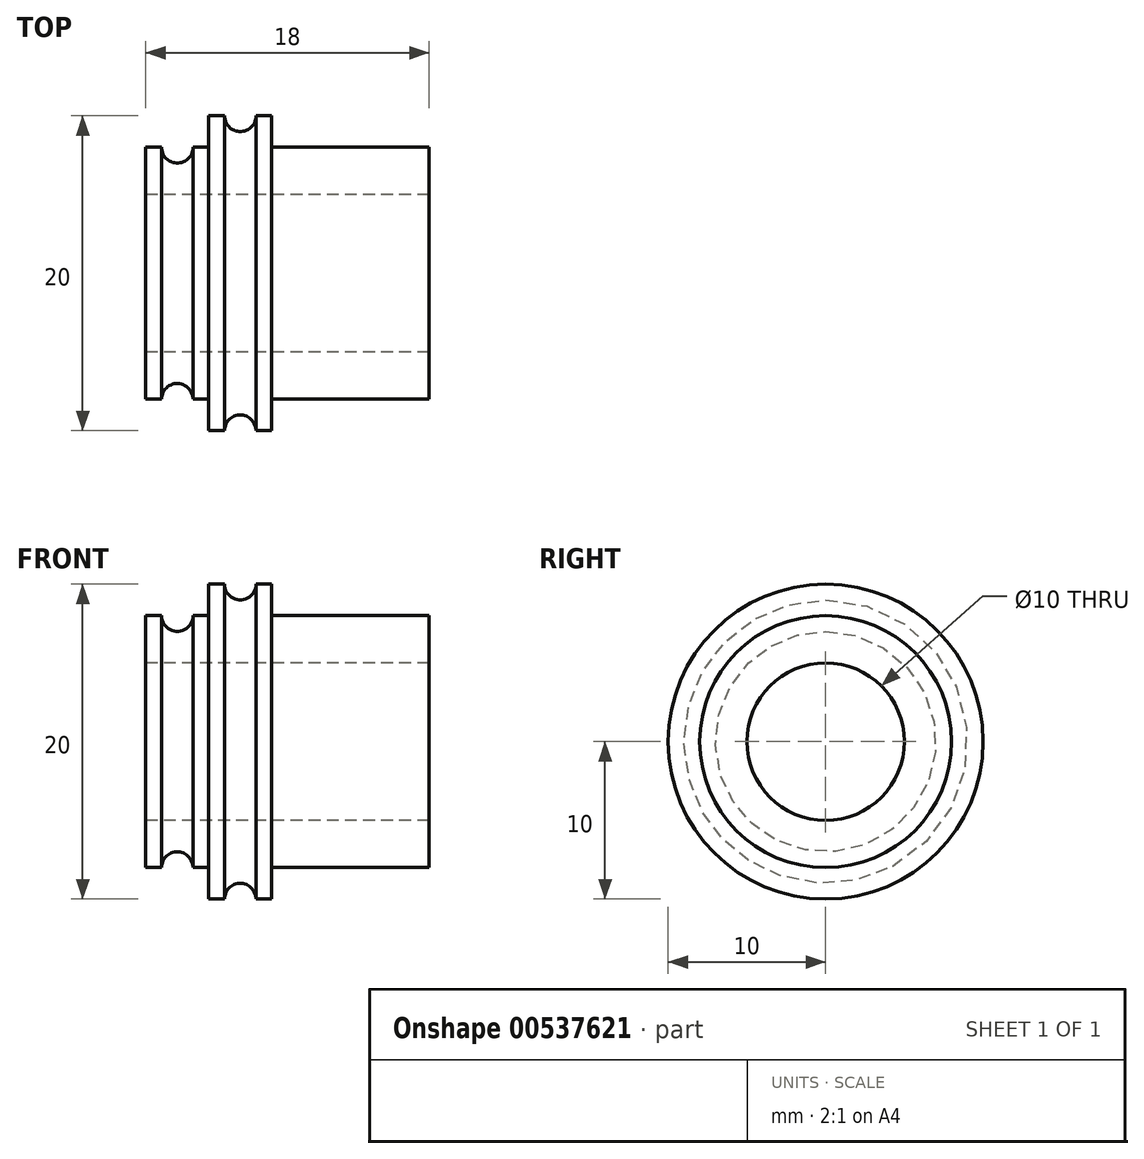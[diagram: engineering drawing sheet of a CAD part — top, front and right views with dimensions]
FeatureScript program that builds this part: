
annotation { "Feature Type Name" : "Feature", "Feature Type Description" : "" }
export const myFeature = defineFeature(function(context is Context, id is Id, definition is map)
    precondition{}
    {
        {
            var Q0;
            Q0=qCreatedBy(makeId("Front.planeOp"),FACE);
            var sketch = newSketch(context, id + "F0", { "sketchPlane" : qUnion([Q0])});
            skLineSegment(sketch, "E0.bottom", {"start": v(0, 5) * mm, "end": v(8, 5) * mm});
            skLineSegment(sketch, "E0.top", {"start": v(4, 10) * mm, "end": v(8, 10) * mm});
            skLineSegment(sketch, "E0.left", {"start": v(0, 5) * mm, "end": v(0, 8) * mm});
            skLineSegment(sketch, "E0.right", {"start": v(8, 5) * mm, "end": v(8, 10) * mm});
            skCircle(sketch, "E1", {"center": v(6, 10) * mm, "radius": 1 * mm});
            skLineSegment(sketch, "E2", {"start": v(0, 0) * mm, "end": v(5.49, 0) * mm});
            skLineSegment(sketch, "E3", {"start": v(0, 8) * mm, "end": v(4, 8) * mm});
            skLineSegment(sketch, "E4", {"start": v(4, 8) * mm, "end": v(4, 10) * mm});
            skPoint(sketch, "E5.orphan", {"position": v(0, 10) * mm});
            skCircle(sketch, "E6", {"center": v(2, 8) * mm, "radius": 1 * mm});
            skSolve(sketch);
        }
        {
            var Q0;
            Q0=makeQuery(id+"F0.imprint","IMPRINT",FACE,{"disambiguationData":[TD([[makeQuery(id+"F0.imprint","IMPRINT",EDGE,{"derivedFrom":sQuery(id+"F0.wireOp",EDGE,"E0.bottom")}),1.0]])]});
            var Q1;
            Q1=sQuery(id+"F0.wireOp",EDGE,"E2");
            revolve(context, id + "F1", {"entities" : qUnion([Q0]), "axis" : qUnion([Q1]), "revolveType" : RevolveType.FULL});
        }
        {
            var Q0;
            Q0=makeQuery(id+"F1.opRevolve","SWEPT_FACE",FACE,{"disambiguationData":[OSD([sQuery(id+"F0.wireOp",EDGE,"E0.right")])]});
            var sketch = newSketch(context, id + "F2", { "sketchPlane" : qUnion([Q0])});
            skCircle(sketch, "E7", {"center": v(0, 0) * mm, "radius": 8 * mm});
            skSolve(sketch);
        }
        {
            var Q0;
            Q0=makeQuery(id+"F2.imprint","IMPRINT",FACE,{"disambiguationData":[TD([[makeQuery(id+"F2.imprint","IMPRINT",EDGE,{"derivedFrom":sQuery(id+"F2.wireOp",EDGE,"E7")}),1.0]])]});
            extrude(context, id + "F3", {"entities" : qUnion([Q0]), "operationType" : NewBodyOperationType.ADD, "depth" : 10 * mm, "offsetDistance" : 25 * mm});
        }
    });
